# Revit family: ГРЕЕРС ЗВ - 100 В
name_source: partatom
category: Wyposażenie mechaniczne
revit_build: Autodesk Revit 2016 (Build: 20150220_1215(x64)
units: mm (PartAtom-declared; Revit-internal decimal feet)

## family parameters
Obiekt nadrzędny = Powierzchnia
Punkt obliczania pomieszczeń = Nie
Tnij formami wycięć po wczytaniu = Nie
Typ części = Normalny
Współdzielony = Nie
Wymiar okrągłego złącza = Użyj średnicy

## types (60) — shared parameters
Bec аппарата, наполненного водой = 20.60 kg
Domyślna rzędna = 2200 mm
IP = 21
Model = ГРЕЕРС ЗВ - 100 В
Opis = Воздушная завеса
Producent = ГРЕЕРС
Автор = www.archispace.com
Вентилятор = Однофазный двигатель с поперечным ротором
Вес аппарата = 19.00 kg
Данные продукта = https://greers.ru
Длина = 1000 mm  [stored 3.28084 ft]
Классификация нагрузки = ДВИГАТЕЛЬ
Коэффициент мощности = 0.94
Макс. потребление тока = 1 A
Материал = ГРЕЕРС-сталь-белый
Материал 2 = ГРЕЕРС-сталь,перфорация-белый
Напряжение питания = 230 V
Патрубки = 3/4"
Полная мощность = 150 VA

## per-type parameters (varying)
| type | Tемпература воды на выходе из теплообменника (Tw2) | Количество воды проходящей через теплообменник | Падение давления воды в теплообменнике | Производительность | Температура воды на входе в теплообменник (Tw1) | Температура воздуха на входе в аппарат (Тр1) | Температура воздуха на выходе из аппарата (Тр2) | Тепловая мощность |
| ГРЕЕРС ЗВ - 100 В, 1 скорость, Tw1/Tw2 = 90/70°C, Tp1 = 0 | 70 °C | 0.174 L/s | 15.4 kPa | 1050 m³/h | 90 °C | 0 °C | 40 °C | 14.2 kW |
| ГРЕЕРС ЗВ - 100 В, 1 скорость, Tw1/Tw2 = 90/70°C, Tp1 = 5 | 70 °C | 0.163 L/s | 13.7 kPa | 1050 m³/h | 90 °C | 5 °C | 42.5 °C | 13.3 kW |
| ГРЕЕРС ЗВ - 100 В, 1 скорость, Tw1/Tw2 = 90/70°C, Tp1 = 10 | 70 °C | 0.152 L/s | 12.1 kPa | 1050 m³/h | 90 °C | 10 °C | 45 °C | 12.4 kW |
| ГРЕЕРС ЗВ - 100 В, 1 скорость, Tw1/Tw2 = 90/70°C, Tp1 = 15 | 70 °C | 0.141 L/s | 10.5 kPa | 1050 m³/h | 90 °C | 15 °C | 47 °C | 11.5 kW |
| ГРЕЕРС ЗВ - 100 В, 1 скорость, Tw1/Tw2 = 90/70°C, Tp1 = 20 | 70 °C | 0.13 L/s | 9.1 kPa | 1050 m³/h | 90 °C | 20 °C | 49.5 °C | 10.6 kW |
| ГРЕЕРС ЗВ - 100 В, 1 скорость, Tw1/Tw2 = 80/60°C, Tp1 = 0 | 60 °C | 0.149 L/s | 12 kPa | 1050 m³/h | 80 °C | 0 °C | 34.5 °C | 12.2 kW |
| ГРЕЕРС ЗВ - 100 В, 1 скорость, Tw1/Tw2 = 80/60°C, Tp1 = 5 | 60 °C | 0.138 L/s | 10.5 kPa | 1050 m³/h | 80 °C | 5 °C | 37 °C | 11.3 kW |
| ГРЕЕРС ЗВ - 100 В, 1 скорость, Tw1/Tw2 = 80/60°C, Tp1 = 10 | 60 °C | 0.127 L/s | 9.1 kPa | 1050 m³/h | 80 °C | 10 °C | 39.5 °C | 10.4 kW |
| ГРЕЕРС ЗВ - 100 В, 1 скорость, Tw1/Tw2 = 80/60°C, Tp1 = 15 | 60 °C | 0.116 L/s | 7.7 kPa | 1050 m³/h | 80 °C | 15 °C | 41.5 °C | 9.5 kW |
| ГРЕЕРС ЗВ - 100 В, 1 скорость, Tw1/Tw2 = 80/60°C, Tp1 = 20 | 60 °C | 0.105 L/s | 6.4 kPa | 1050 m³/h | 80 °C | 20 °C | 44 °C | 8.6 kW |
| ГРЕЕРС ЗВ - 100 В, 1 скорость, Tw1/Tw2 = 70/50°C, Tp1 = 0 | 50 °C | 0.125 L/s | 9 kPa | 1050 m³/h | 70 °C | 0 °C | 29 °C | 10.3 kW |
| ГРЕЕРС ЗВ - 100 В, 1 скорость, Tw1/Tw2 = 70/50°C, Tp1 = 5 | 50 °C | 0.114 L/s | 7.7 kPa | 1050 m³/h | 70 °C | 5 °C | 31.5 °C | 9.4 kW |
| ГРЕЕРС ЗВ - 100 В, 1 скорость, Tw1/Tw2 = 70/50°C, Tp1 = 10 | 50 °C | 0.103 L/s | 6.4 kPa | 1050 m³/h | 70 °C | 10 °C | 33.5 °C | 8.5 kW |
| ГРЕЕРС ЗВ - 100 В, 1 скорость, Tw1/Tw2 = 70/50°C, Tp1 = 15 | 50 °C | 0.092 L/s | 5.2 kPa | 1050 m³/h | 70 °C | 15 °C | 36 °C | 7.5 kW |
| ГРЕЕРС ЗВ - 100 В, 1 скорость, Tw1/Tw2 = 70/50°C, Tp1 = 20 | 50 °C | 0.08 L/s | 4.1 kPa | 1050 m³/h | 70 °C | 20 °C | 38.5 °C | 6.6 kW |
| ГРЕЕРС ЗВ - 100 В, 1 скорость, Tw1/Tw2 = 60/40°C, Tp1 = 0 | 40 °C | 0.1 L/s | 6.4 kPa | 1050 m³/h | 60 °C | 0 °C | 23.5 °C | 8.3 kW |
| ГРЕЕРС ЗВ - 100 В, 1 скорость, Tw1/Tw2 = 60/40°C, Tp1 = 5 | 40 °C | 0.089 L/s | 5.2 kPa | 1050 m³/h | 60 °C | 5 °C | 26 °C | 7.4 kW |
| ГРЕЕРС ЗВ - 100 В, 1 скорость, Tw1/Tw2 = 60/40°C, Tp1 = 10 | 40 °C | 0.078 L/s | 4.1 kPa | 1050 m³/h | 60 °C | 10 °C | 28 °C | 6.5 kW |
| ГРЕЕРС ЗВ - 100 В, 1 скорость, Tw1/Tw2 = 60/40°C, Tp1 = 15 | 40 °C | 0.067 L/s | 3.1 kPa | 1050 m³/h | 60 °C | 15 °C | 30.5 °C | 5.5 kW |
| ГРЕЕРС ЗВ - 100 В, 1 скорость, Tw1/Tw2 = 60/40°C, Tp1 = 20 | 40 °C | 0.055 L/s | 2.2 kPa | 1050 m³/h | 60 °C | 20 °C | 32.5 °C | 4.6 kW |
| ГРЕЕРС ЗВ - 100 В, 2 скорость, Tw1/Tw2 = 90/70°C, Tp1 = 0 | 70 °C | 0.194 L/s | 18.8 kPa | 1250 m³/h | 90 °C | 0 °C | 37.5 °C | 15.8 kW |
| ГРЕЕРС ЗВ - 100 В, 2 скорость, Tw1/Tw2 = 90/70°C, Tp1 = 5 | 70 °C | 0.182 L/s | 16.7 kPa | 1250 m³/h | 90 °C | 5 °C | 40 °C | 14.8 kW |
| ГРЕЕРС ЗВ - 100 В, 2 скорость, Tw1/Tw2 = 90/70°C, Tp1 = 10 | 70 °C | 0.17 L/s | 14.7 kPa | 1250 m³/h | 90 °C | 10 °C | 42.5 °C | 13.8 kW |
| ГРЕЕРС ЗВ - 100 В, 2 скорость, Tw1/Tw2 = 90/70°C, Tp1 = 15 | 70 °C | 0.157 L/s | 12.9 kPa | 1250 m³/h | 90 °C | 15 °C | 45 °C | 12.8 kW |
| ГРЕЕРС ЗВ - 100 В, 2 скорость, Tw1/Tw2 = 90/70°C, Tp1 = 20 | 70 °C | 0.145 L/s | 11.1 kPa | 1250 m³/h | 90 °C | 20 °C | 47.5 °C | 11.8 kW |
| ГРЕЕРС ЗВ - 100 В, 2 скорость, Tw1/Tw2 = 80/60°C, Tp1 = 0 | 60 °C | 0.166 L/s | 14.7 kPa | 1250 m³/h | 80 °C | 0 °C | 32.5 °C | 13.6 kW |
| ГРЕЕРС ЗВ - 100 В, 2 скорость, Tw1/Tw2 = 80/60°C, Tp1 = 5 | 60 °C | 0.154 L/s | 12.8 kPa | 1250 m³/h | 80 °C | 5 °C | 35 °C | 12.7 kW |
| ГРЕЕРС ЗВ - 100 В, 2 скорость, Tw1/Tw2 = 80/60°C, Tp1 = 10 | 60 °C | 0.142 L/s | 11 kPa | 1250 m³/h | 80 °C | 10 °C | 37.5 °C | 11.6 kW |
| ГРЕЕРС ЗВ - 100 В, 2 скорость, Tw1/Tw2 = 80/60°C, Tp1 = 15 | 60 °C | 0.13 L/s | 9.4 kPa | 1250 m³/h | 80 °C | 15 °C | 40 °C | 10.6 kW |
| ГРЕЕРС ЗВ - 100 В, 2 скорость, Tw1/Tw2 = 80/60°C, Tp1 = 20 | 60 °C | 0.117 L/s | 7.8 kPa | 1250 m³/h | 80 °C | 20 °C | 42.5 °C | 9.6 kW |
| ГРЕЕРС ЗВ - 100 В, 2 скорость, Tw1/Tw2 = 70/50°C, Tp1 = 0 | 50 °C | 0.139 L/s | 11 kPa | 1250 m³/h | 70 °C | 0 °C | 27 °C | 11.5 kW |
| ГРЕЕРС ЗВ - 100 В, 2 скорость, Tw1/Tw2 = 70/50°C, Tp1 = 5 | 50 °C | 0.127 L/s | 9.3 kPa | 1250 m³/h | 70 °C | 5 °C | 29.5 °C | 10.5 kW |
| ГРЕЕРС ЗВ - 100 В, 2 скорость, Tw1/Tw2 = 70/50°C, Tp1 = 10 | 50 °C | 0.115 L/s | 7.8 kPa | 1250 m³/h | 70 °C | 10 °C | 32 °C | 9.4 kW |
| ГРЕЕРС ЗВ - 100 В, 2 скорость, Tw1/Tw2 = 70/50°C, Tp1 = 15 | 50 °C | 0.102 L/s | 6.3 kPa | 1250 m³/h | 70 °C | 15 °C | 35 °C | 8.4 kW |
| ГРЕЕРС ЗВ - 100 В, 2 скорость, Tw1/Tw2 = 70/50°C, Tp1 = 20 | 50 °C | 0.09 L/s | 5 kPa | 1250 m³/h | 70 °C | 20 °C | 37.5 °C | 7.4 kW |
| ГРЕЕРС ЗВ - 100 В, 2 скорость, Tw1/Tw2 = 60/40°C, Tp1 = 0 | 40 °C | 0.112 L/s | 7.8 kPa | 1250 m³/h | 60 °C | 0 °C | 22 °C | 9.3 kW |
| ГРЕЕРС ЗВ - 100 В, 2 скорость, Tw1/Tw2 = 60/40°C, Tp1 = 5 | 40 °C | 0.1 L/s | 6.3 kPa | 1250 m³/h | 60 °C | 5 °C | 24.5 °C | 8.2 kW |
| ГРЕЕРС ЗВ - 100 В, 2 скорость, Tw1/Tw2 = 60/40°C, Tp1 = 10 | 40 °C | 0.087 L/s | 5 kPa | 1250 m³/h | 60 °C | 10 °C | 27 °C | 7.2 kW |
| ГРЕЕРС ЗВ - 100 В, 2 скорость, Tw1/Tw2 = 60/40°C, Tp1 = 15 | 40 °C | 0.075 L/s | 3.8 kPa | 1250 m³/h | 60 °C | 15 °C | 29.5 °C | 6.2 kW |
| ГРЕЕРС ЗВ - 100 В, 2 скорость, Tw1/Tw2 = 60/40°C, Tp1 = 20 | 40 °C | 0.062 L/s | 2.7 kPa | 1250 m³/h | 60 °C | 20 °C | 32 °C | 5.1 kW |
| ГРЕЕРС ЗВ - 100 В, 3 скорость, Tw1/Tw2 = 90/70°C, Tp1 = 0 | 70 °C | 0.208 L/s | 21.3 kPa | 1400 m³/h | 90 °C | 0 °C | 36 °C | 17 kW |
| ГРЕЕРС ЗВ - 100 В, 3 скорость, Tw1/Tw2 = 90/70°C, Tp1 = 5 | 70 °C | 0.195 L/s | 19 kPa | 1400 m³/h | 90 °C | 5 °C | 38.5 °C | 15.9 kW |
| ГРЕЕРС ЗВ - 100 В, 3 скорость, Tw1/Tw2 = 90/70°C, Tp1 = 10 | 70 °C | 0.182 L/s | 16.7 kPa | 1400 m³/h | 90 °C | 10 °C | 41 °C | 14.9 kW |
| ГРЕЕРС ЗВ - 100 В, 3 скорость, Tw1/Tw2 = 90/70°C, Tp1 = 15 | 70 °C | 0.169 L/s | 14.6 kPa | 1400 m³/h | 90 °C | 15 °C | 44 °C | 13.8 kW |
| ГРЕЕРС ЗВ - 100 В, 3 скорость, Tw1/Tw2 = 90/70°C, Tp1 = 20 | 70 °C | 0.156 L/s | 12.6 kPa | 1400 m³/h | 90 °C | 20 °C | 46.5 °C | 12.7 kW |
| ГРЕЕРС ЗВ - 100 В, 3 скорость, Tw1/Tw2 = 80/60°C, Tp1 = 0 | 60 °C | 0.179 L/s | 16.7 kPa | 1400 m³/h | 80 °C | 0 °C | 31 °C | 14.6 kW |
| ГРЕЕРС ЗВ - 100 В, 3 скорость, Tw1/Tw2 = 80/60°C, Tp1 = 5 | 60 °C | 0.166 L/s | 14.5 kPa | 1400 m³/h | 80 °C | 5 °C | 33.5 °C | 13.6 kW |
| ГРЕЕРС ЗВ - 100 В, 3 скорость, Tw1/Tw2 = 80/60°C, Tp1 = 10 | 60 °C | 0.152 L/s | 12.5 kPa | 1400 m³/h | 80 °C | 10 °C | 36.5 °C | 12.5 kW |
| ГРЕЕРС ЗВ - 100 В, 3 скорость, Tw1/Tw2 = 80/60°C, Tp1 = 15 | 60 °C | 0.139 L/s | 10.6 kPa | 1400 m³/h | 80 °C | 15 °C | 39 °C | 11.4 kW |
| ГРЕЕРС ЗВ - 100 В, 3 скорость, Tw1/Tw2 = 80/60°C, Tp1 = 20 | 60 °C | 0.126 L/s | 8.9 kPa | 1400 m³/h | 80 °C | 20 °C | 41.5 °C | 10.3 kW |
| ГРЕЕРС ЗВ - 100 В, 3 скорость, Tw1/Tw2 = 70/50°C, Tp1 = 0 | 50 °C | 0.149 L/s | 12.5 kPa | 1400 m³/h | 70 °C | 0 °C | 26 °C | 12.3 kW |
| ГРЕЕРС ЗВ - 100 В, 3 скорость, Tw1/Tw2 = 70/50°C, Tp1 = 5 | 50 °C | 0.136 L/s | 10.6 kPa | 1400 m³/h | 70 °C | 5 °C | 28.5 °C | 11.2 kW |
| ГРЕЕРС ЗВ - 100 В, 3 скорость, Tw1/Tw2 = 70/50°C, Tp1 = 10 | 50 °C | 0.123 L/s | 8.8 kPa | 1400 m³/h | 70 °C | 10 °C | 31.5 °C | 10.1 kW |
| ГРЕЕРС ЗВ - 100 В, 3 скорость, Tw1/Tw2 = 70/50°C, Tp1 = 15 | 50 °C | 0.11 L/s | 7.2 kPa | 1400 m³/h | 70 °C | 15 °C | 34 °C | 9 kW |
| ГРЕЕРС ЗВ - 100 В, 3 скорость, Tw1/Tw2 = 70/50°C, Tp1 = 20 | 50 °C | 0.096 L/s | 5.7 kPa | 1400 m³/h | 70 °C | 20 °C | 36.5 °C | 7.9 kW |
| ГРЕЕРС ЗВ - 100 В, 3 скорость, Tw1/Tw2 = 60/40°C, Tp1 = 0 | 40 °C | 0.12 L/s | 8.8 kPa | 1400 m³/h | 60 °C | 0 °C | 21 °C | 9.9 kW |
| ГРЕЕРС ЗВ - 100 В, 3 скорость, Tw1/Tw2 = 60/40°C, Tp1 = 5 | 40 °C | 0.107 L/s | 7.1 kPa | 1400 m³/h | 60 °C | 5 °C | 23.5 °C | 8.8 kW |
| ГРЕЕРС ЗВ - 100 В, 3 скорость, Tw1/Tw2 = 60/40°C, Tp1 = 10 | 40 °C | 0.094 L/s | 5.6 kPa | 1400 m³/h | 60 °C | 10 °C | 26.5 °C | 7.7 kW |
| ГРЕЕРС ЗВ - 100 В, 3 скорость, Tw1/Tw2 = 60/40°C, Tp1 = 15 | 40 °C | 0.08 L/s | 4.3 kPa | 1400 m³/h | 60 °C | 15 °C | 29 °C | 6.6 kW |
| ГРЕЕРС ЗВ - 100 В, 3 скорость, Tw1/Tw2 = 60/40°C, Tp1 = 20 | 40 °C | 0.066 L/s | 3.1 kPa | 1400 m³/h | 60 °C | 20 °C | 31.5 °C | 5.5 kW |

note: [stored X ft] marks values corroborated as IEEE doubles in the binary element streams (Revit-internal decimal feet)
